FREECAD ASSEMBLY — COMPONENT RECIPES ("robot-main")

This assembly document has 11 components, labeled P0..P10 below (a component is one placed body or linked part). 6 of them carry a construction recipe — the FreeCAD feature program that regenerates the part from scratch, quoted from this document or its linked companion documents; the rest are supplied as boundary geometry only. No exploded tour is included for this assembly.
COMPONENT P0 — geometry summary ("traction-assy-l"; no construction recipe available for this part):
  bounding box: 33.4 x 17.5 x 10.2 mm
  tessellated surface: 1,796 triangles
  volume: 1266 mm^3 (21% of its bounding box)
  symmetry: mirror-symmetric across its y mid-plane
COMPONENT P1 — recipe-attached ("battery-t", a linked part whose construction recipe lives in a companion FreeCAD document of the same project; that document's serialized recipe follows).
Construction recipe (the companion document, serialized — sketch geometry with constraints, then the solid features built on it; lengths are millimeters unless a unit is written):

FCSTD DOCUMENT  (FreeCAD 0.21R33668 +7 (Git))
Label: BL-5C
License: All rights reserved
LicenseURL: https://en.wikipedia.org/wiki/All_rights_reserved
objects: Sketcher::SketchObject×2, PartDesign::Pad×1, PartDesign::Plane×1, PartDesign::Pocket×1, PartDesign::Body×1
note: 8 computed .brp shape members not serialized (recipe doc carries the construction recipe); baked Part::Feature solids carry a one-line shape summary decoded from their .brp

FEATURE [Sketcher::SketchObject] Sketch
  FullyConstrained = true
  MapMode = 5
  Placement = pos=(0,0,0) rot=(0.57735,0.57735,0.57735;2.0944rad)
  Support = -> [YZ_Plane]
  sketch-geometry (6):
    g0: ArcOfCircle CenterX=-14.15 CenterY=0 CenterZ=0 NormalX=0 NormalY=0 NormalZ=1 AngleXU=0 Radius=2.8 StartAngle=1.5708 EndAngle=4.71239
    g1: ArcOfCircle CenterX=14.15 CenterY=0 CenterZ=0 NormalX=0 NormalY=0 NormalZ=1 AngleXU=0 Radius=2.8 StartAngle=4.71239 EndAngle=7.85398
    g2: LineSegment StartX=-14.15 StartY=2.8 StartZ=0 EndX=14.15 EndY=2.8 EndZ=0
    g3: LineSegment StartX=-14.15 StartY=-2.8 StartZ=0 EndX=14.15 EndY=-2.8 EndZ=0
    g4: GeomPoint X=16.95 Y=0 Z=0
    g5: GeomPoint X=-16.95 Y=0 Z=0
  constraints (13):
    c: PointOnObject(g0,g-1)
    c: Horizontal(g2)
    c: Tangent(g2,g0) = 1.5708
    c: Tangent(g3,g0) = -1.5708
    c: Tangent(g3,g1) = -1.5708
    c: Tangent(g2,g1) = 1.5708
    c: PointOnObject(g4,g1)
    c: PointOnObject(g4,g-1)
    c: DistanceY(g1,g1) = 5.6
    c: Symmetric(g0,g1,g-1)
    c: PointOnObject(g5,g0)
    c: PointOnObject(g5,g-1)
    c: DistanceX(g5,g4) = 33.9
FEATURE [PartDesign::Pad] Pad
  Direction = (1,-2e-16,3e-16)
  Length = 53
  Length2 = 10
  Placement = pos=(0,0,0) rot=(0.57735,0.57735,0.57735;2.0944rad)
  Profile = -> Sketch
  ReferenceAxis = -> Sketch [N_Axis]
  Type = 0
FEATURE [PartDesign::Plane] DatumPlane
  Length = 60
  MapMode = 5
  Placement = pos=(0,0,0) rot=(0.57735,0.57735,-0.57735;4.18879rad)
  ResizeMode = 0
  Support = -> [Pad]
  Width = 60
FEATURE [Sketcher::SketchObject] Sketch001
  ExternalGeometry = -> [Pad]
  FullyConstrained = true
  MapMode = 5
  Placement = pos=(0,0,0) rot=(0.57735,0.57735,-0.57735;4.18879rad)
  Support = -> [DatumPlane]
  sketch-geometry (16):
    g0: LineSegment StartX=11.95 StartY=2.3 StartZ=0 EndX=13.95 EndY=2.3 EndZ=0
    g1: LineSegment StartX=13.95 StartY=2.3 StartZ=0 EndX=13.95 EndY=-2.3 EndZ=0
    g2: LineSegment StartX=13.95 StartY=-2.3 StartZ=0 EndX=11.95 EndY=-2.3 EndZ=0
    g3: LineSegment StartX=11.95 StartY=-2.3 StartZ=0 EndX=11.95 EndY=2.3 EndZ=0
    g4: LineSegment StartX=8.75 StartY=2.3 StartZ=0 EndX=10.75 EndY=2.3 EndZ=0
    g5: LineSegment StartX=10.75 StartY=2.3 StartZ=0 EndX=10.75 EndY=-2.3 EndZ=0
    g6: LineSegment StartX=10.75 StartY=-2.3 StartZ=0 EndX=8.75 EndY=-2.3 EndZ=0
    g7: LineSegment StartX=8.75 StartY=-2.3 StartZ=0 EndX=8.75 EndY=2.3 EndZ=0
    g8: LineSegment StartX=5.55 StartY=2.3 StartZ=0 EndX=7.55 EndY=2.3 EndZ=0
    g9: LineSegment StartX=7.55 StartY=2.3 StartZ=0 EndX=7.55 EndY=-2.3 EndZ=0
    g10: LineSegment StartX=7.55 StartY=-2.3 StartZ=0 EndX=5.55 EndY=-2.3 EndZ=0
    g11: LineSegment StartX=5.55 StartY=-2.3 StartZ=0 EndX=5.55 EndY=2.3 EndZ=0
    g12: LineSegment StartX=7.55 StartY=2.3 StartZ=0 EndX=8.75 EndY=2.3 EndZ=0
    g13: LineSegment StartX=10.75 StartY=2.3 StartZ=0 EndX=11.95 EndY=2.3 EndZ=0
    g14: GeomPoint X=-16.95 Y=0 Z=0
    g15: GeomPoint X=16.95 Y=0 Z=0
  constraints (43):
    c: Coincident(g0,g1)
    c: Coincident(g1,g2)
    c: Coincident(g2,g3)
    c: Coincident(g3,g0)
    c: Horizontal(g0)
    c: Horizontal(g2)
    c: Vertical(g3)
    c: Coincident(g4,g5)
    c: Coincident(g5,g6)
    c: Coincident(g6,g7)
    c: Coincident(g7,g4)
    c: Horizontal(g4)
    c: Horizontal(g6)
    c: Vertical(g5)
    c: Vertical(g7)
    c: Coincident(g8,g9)
    c: Coincident(g9,g10)
    c: Coincident(g10,g11)
    c: Coincident(g11,g8)
    c: Horizontal(g8)
    c: Horizontal(g10)
    c: Vertical(g9)
    c: Vertical(g11)
    c: PointOnObject(g4,g8)
    c: PointOnObject(g0,g8)
    c: PointOnObject(g6,g10)
    c: PointOnObject(g2,g10)
    c: Equal(g8,g4)
    c: Coincident(g12,g8)
    c: Coincident(g12,g4)
    c: Coincident(g13,g4)
    c: Coincident(g13,g0)
    c: Equal(g13,g12)
    c: PointOnObject(g14,g-3)
    c: PointOnObject(g14,g-1)
    c: DistanceX(g14,g10) = 22.5
    c: PointOnObject(g15,g-1)
    c: PointOnObject(g15,g-4)
    c: DistanceX(g1,g15) = 3
    c: DistanceX(g6,g6) = 2
    c: Equal(g2,g6)
    c: Symmetric(g0,g1,g-1)
    c: DistanceY(g1,g1) = 4.6
FEATURE [PartDesign::Pocket] Pocket
  BaseFeature = -> Pad
  Direction = (1,-4e-16,4e-16)
  Length = 0.6
  Length2 = 5
  Placement = pos=(0,0,0) rot=(0.57735,0.57735,0.57735;2.0944rad)
  Profile = -> Sketch001
  ReferenceAxis = -> Sketch001 [N_Axis]
  Type = 0
FEATURE [PartDesign::Body] Body  label="BL-5C"
  Group = -> [Sketch,Pad,DatumPlane,Sketch001,Pocket]
  Origin = -> Origin
  Tip = -> Pocket
COMPONENT P2 — same part as P1; its construction recipe is shown at P1.
COMPONENT P3 — recipe-attached ("pcb", a linked part whose construction recipe lives in a companion FreeCAD document of the same project; that document's serialized recipe follows).
Construction recipe (the companion document, serialized — sketch geometry with constraints, then the solid features built on it; lengths are millimeters unless a unit is written):

FCSTD DOCUMENT  (FreeCAD 0.21R33668 +7 (Git))
Label: robot-pcb
License: All rights reserved
LicenseURL: https://en.wikipedia.org/wiki/All_rights_reserved
objects: Part::Feature×12, App::Part×12, Sketcher::SketchObject×2, PartDesign::Pad×2, PartDesign::Body×2, App::LinkGroup×1
note: 20 computed .brp shape members not serialized (recipe doc carries the construction recipe); baked Part::Feature solids carry a one-line shape summary decoded from their .brp

FEATURE [Sketcher::SketchObject] Sketch004
  FullyConstrained = true
  MapMode = 5
  Support = -> [XY_Plane001]
  sketch-geometry (40):
    g0: LineSegment StartX=-32 StartY=20 StartZ=0 EndX=32 EndY=20 EndZ=0
    g1: LineSegment StartX=32 StartY=20 StartZ=0 EndX=32 EndY=-20 EndZ=0
    g2: LineSegment StartX=32 StartY=-20 StartZ=0 EndX=-32 EndY=-20 EndZ=0
    g3: LineSegment StartX=-32 StartY=-20 StartZ=0 EndX=-32 EndY=20 EndZ=0
    g4: LineSegment StartX=32 StartY=20 StartZ=0 EndX=32 EndY=-20 EndZ=0
    g5: ArcOfCircle CenterX=13 CenterY=-15 CenterZ=0 NormalX=0 NormalY=0 NormalZ=1 AngleXU=0 Radius=1.05 StartAngle=1.5708 EndAngle=4.71239
    g6: ArcOfCircle CenterX=30 CenterY=-15 CenterZ=0 NormalX=0 NormalY=0 NormalZ=1 AngleXU=0 Radius=1.05 StartAngle=4.71239 EndAngle=7.85398
    g7: LineSegment StartX=13 StartY=-16.05 StartZ=0 EndX=30 EndY=-16.05 EndZ=0
    g8: LineSegment StartX=30 StartY=-13.95 StartZ=0 EndX=13 EndY=-13.95 EndZ=0
    g9: ArcOfCircle CenterX=-30 CenterY=15 CenterZ=0 NormalX=0 NormalY=0 NormalZ=1 AngleXU=0 Radius=1.05 StartAngle=1.5708 EndAngle=4.71239
    g10: ArcOfCircle CenterX=-13 CenterY=15 CenterZ=0 NormalX=0 NormalY=0 NormalZ=1 AngleXU=0 Radius=1.05 StartAngle=4.71239 EndAngle=7.85398
    g11: LineSegment StartX=-30 StartY=13.95 StartZ=0 EndX=-13 EndY=13.95 EndZ=0
    g12: LineSegment StartX=-13 StartY=16.05 StartZ=0 EndX=-30 EndY=16.05 EndZ=0
    g13: LineSegment StartX=-32 StartY=-20 StartZ=0 EndX=-32 EndY=20 EndZ=0
    g14: ArcOfCircle CenterX=4 CenterY=15 CenterZ=0 NormalX=0 NormalY=0 NormalZ=1 AngleXU=0 Radius=1.05 StartAngle=1.5708 EndAngle=4.71239
    g15: ArcOfCircle CenterX=24 CenterY=15 CenterZ=0 NormalX=0 NormalY=0 NormalZ=1 AngleXU=0 Radius=1.05 StartAngle=4.71239 EndAngle=7.85398
    g16: LineSegment StartX=4 StartY=13.95 StartZ=0 EndX=24 EndY=13.95 EndZ=0
    g17: LineSegment StartX=24 StartY=16.05 StartZ=0 EndX=4 EndY=16.05 EndZ=0
    g18: ArcOfCircle CenterX=-24 CenterY=-15 CenterZ=0 NormalX=0 NormalY=0 NormalZ=1 AngleXU=0 Radius=1.05 StartAngle=1.5708 EndAngle=4.71239
    g19: ArcOfCircle CenterX=-4 CenterY=-15 CenterZ=0 NormalX=0 NormalY=0 NormalZ=1 AngleXU=0 Radius=1.05 StartAngle=4.71239 EndAngle=7.85398
    g20: LineSegment StartX=-24 StartY=-16.05 StartZ=0 EndX=-4 EndY=-16.05 EndZ=0
    g21: LineSegment StartX=-4 StartY=-13.95 StartZ=0 EndX=-24 EndY=-13.95 EndZ=0
    g22: ArcOfCircle CenterX=-61 CenterY=0 CenterZ=0 NormalX=0 NormalY=0 NormalZ=1 AngleXU=0 Radius=29 StartAngle=5.75173 EndAngle=6.81464
    g23: LineSegment StartX=-36 StartY=14.6969 StartZ=0 EndX=-36 EndY=20 EndZ=0
    g24: LineSegment StartX=-32 StartY=20 StartZ=0 EndX=-36 EndY=20 EndZ=0
    g25: LineSegment StartX=-36 StartY=-14.6969 StartZ=0 EndX=-36 EndY=-20 EndZ=0
    g26: LineSegment StartX=-32 StartY=-20 StartZ=0 EndX=-36 EndY=-20 EndZ=0
    g27: ArcOfCircle CenterX=61 CenterY=0 CenterZ=0 NormalX=0 NormalY=0 NormalZ=1 AngleXU=0 Radius=29 StartAngle=2.61013 EndAngle=3.67305
    g28: LineSegment StartX=32 StartY=20 StartZ=0 EndX=36 EndY=20 EndZ=0
    g29: LineSegment StartX=36 StartY=20 StartZ=0 EndX=36 EndY=14.6969 EndZ=0
    g30: LineSegment StartX=32 StartY=-20 StartZ=0 EndX=36 EndY=-20 EndZ=0
    g31: LineSegment StartX=36 StartY=-20 StartZ=0 EndX=36 EndY=-14.6969 EndZ=0
    g32: Circle CenterX=-33.5 CenterY=-17.5 CenterZ=0 NormalX=0 NormalY=0 NormalZ=1 AngleXU=0 Radius=1.3
    g33: Circle CenterX=-33.5 CenterY=17.5 CenterZ=0 NormalX=0 NormalY=0 NormalZ=1 AngleXU=0 Radius=1.3
    g34: Circle CenterX=33.5 CenterY=17.5 CenterZ=0 NormalX=0 NormalY=0 NormalZ=1 AngleXU=0 Radius=1.3
    g35: Circle CenterX=33.5 CenterY=-17.5 CenterZ=0 NormalX=0 NormalY=0 NormalZ=1 AngleXU=0 Radius=1.3
    g36: LineSegment StartX=-33.5 StartY=17.5 StartZ=0 EndX=33.5 EndY=17.5 EndZ=0
    g37: LineSegment StartX=33.5 StartY=17.5 StartZ=0 EndX=33.5 EndY=-17.5 EndZ=0
    g38: LineSegment StartX=33.5 StartY=-17.5 StartZ=0 EndX=-33.5 EndY=-17.5 EndZ=0
    g39: LineSegment StartX=-33.5 StartY=-17.5 StartZ=0 EndX=-33.5 EndY=17.5 EndZ=0
  constraints (104):
    c: Coincident(g0,g1)
    c: Coincident(g1,g2)
    c: Coincident(g2,g3)
    c: Coincident(g3,g0)
    c: Horizontal(g0)
    c: Horizontal(g2)
    c: Vertical(g1)
    c: Vertical(g3)
    c: Symmetric(g0,g1,g-1)
    c: DistanceY(g1,g1) = 40
    c: DistanceX(g0,g0) = 64
    c: Coincident(g4,g2)
    c: Tangent(g5,g7) = -1.5708
    c: Tangent(g7,g6) = -1.5708
    c: Tangent(g6,g8) = -1.5708
    c: Tangent(g8,g5) = -1.5708
    c: Equal(g5,g6)
    c: Horizontal(g7)
    c: DistanceX(g5,g6) = 17
    c: DistanceY(g2,g6) = 5
    c: DistanceY(g5,g5) = 2.1
    c: DistanceX(g6,g2) = 2
    c: Tangent(g9,g11) = -1.5708
    c: Tangent(g11,g10) = -1.5708
    c: Tangent(g10,g12) = -1.5708
    c: Tangent(g12,g9) = -1.5708
    c: Equal(g9,g10)
    c: Horizontal(g11)
    c: Equal(g10,g5)
    c: Symmetric(g9,g6,g-1)
    c: Coincident(g13,g0)
    c: DistanceY(g10,g10) = 2.1
    c: DistanceY(g6,g0) = 35
    c: Coincident(g13,g2)
    c: Coincident(g4,g0)
    c: Tangent(g14,g16) = -1.5708
    c: Tangent(g16,g15) = -1.5708
    c: Tangent(g15,g17) = -1.5708
    c: Tangent(g17,g14) = -1.5708
    c: Equal(g14,g15)
    c: Horizontal(g16)
    c: Tangent(g18,g20) = -1.5708
    c: Tangent(g20,g19) = -1.5708
    c: Tangent(g19,g21) = -1.5708
    c: Tangent(g21,g18) = -1.5708
    c: Equal(g18,g19)
    c: Horizontal(g20)
    c: Equal(g19,g10)
    c: Equal(g14,g10)
    c: PointOnObject(g14,g12)
    c: Symmetric(g18,g15,g-1)
    c: DistanceX(g2,g18) = 8
    c: PointOnObject(g22,g-1)
    c: Tangent(g22,g13)
    c: Diameter(g22) = 58
    c: Coincident(g23,g22)
    c: Vertical(g23)
    c: Coincident(g24,g0)
    c: Coincident(g24,g23)
    c: Coincident(g25,g22)
    c: Vertical(g25)
    c: Coincident(g26,g2)
    c: Coincident(g26,g25)
    c: Horizontal(g26)
    c: Horizontal(g24)
    c: Equal(g24,g26)
    c: DistanceX(g26,g26) = 4
    c: PointOnObject(g27,g-1)
    c: Tangent(g27,g4)
    c: Coincident(g0,g28)
    c: Horizontal(g28)
    c: Coincident(g28,g29)
    c: Coincident(g29,g27)
    c: Vertical(g29)
    c: Coincident(g2,g30)
    c: Horizontal(g30)
    c: Coincident(g30,g31)
    c: Coincident(g31,g27)
    c: Vertical(g31)
    c: Equal(g30,g28)
    c: Diameter(g27) = 58
    c: DistanceX(g30,g30) = 4
    c: Coincident(g36,g37)
    c: Coincident(g37,g38)
    c: Coincident(g38,g39)
    c: Coincident(g39,g36)
    c: Horizontal(g36)
    c: Horizontal(g38)
    c: Vertical(g37)
    c: Vertical(g39)
    c: Coincident(g36,g33)
    c: Coincident(g37,g35)
    c: Coincident(g36,g34)
    c: Coincident(g38,g32)
    c: Symmetric(g32,g34,g-1)
    c: Diameter(g33) = 2.6
    c: Equal(g35,g32)
    c: Equal(g32,g34)
    c: Equal(g34,g33)
    c: DistanceX(g36,g36) = 67
    c: DistanceY(g39,g39) = 35
    c: Equal(g21,g17)
    c: Equal(g12,g8)
    c: DistanceX(g14,g15) = 20
FEATURE [PartDesign::Pad] Pad005
  Direction = (0,0,1)
  Length = 1.6
  Length2 = 10
  Profile = -> Sketch004
  ReferenceAxis = -> Sketch004 [N_Axis]
  Type = 0
FEATURE [PartDesign::Body] Body001  label="motor-pcb"
  Group = -> [Sketch004,Pad005]
  Origin = -> Origin001
  Placement = pos=(0,0,7) rot=(0,0,1;0rad)
  Tip = -> Pad005
FEATURE [Sketcher::SketchObject] Sketch005
  FullyConstrained = true
  MapMode = 5
  Support = -> [XY_Plane002]
  sketch-geometry (4):
    g0: LineSegment StartX=-32 StartY=20 StartZ=0 EndX=32 EndY=20 EndZ=0
    g1: LineSegment StartX=32 StartY=20 StartZ=0 EndX=32 EndY=-20 EndZ=0
    g2: LineSegment StartX=32 StartY=-20 StartZ=0 EndX=-32 EndY=-20 EndZ=0
    g3: LineSegment StartX=-32 StartY=-20 StartZ=0 EndX=-32 EndY=20 EndZ=0
  constraints (11):
    c: Coincident(g0,g1)
    c: Coincident(g1,g2)
    c: Coincident(g2,g3)
    c: Coincident(g3,g0)
    c: Horizontal(g0)
    c: Horizontal(g2)
    c: Vertical(g1)
    c: Vertical(g3)
    c: Symmetric(g0,g1,g-1)
    c: DistanceY(g1,g1) = 40
    c: DistanceX(g0,g0) = 64
FEATURE [PartDesign::Pad] Pad006
  Direction = (0,0,1)
  Length = 1.6
  Length2 = 10
  Profile = -> Sketch005
  ReferenceAxis = -> Sketch005 [N_Axis]
  Type = 0
FEATURE [PartDesign::Body] Body002  label="logic-pcb"
  Group = -> [Sketch005,Pad006]
  Origin = -> Origin002
  Placement = pos=(0,0,-7) rot=(0,1,0;3.14159rad)
  Tip = -> Pad006
FEATURE [Part::Feature] Part__Feature016  label="SOLID012"
  shape: bbox 11.3 x 3.89 x 7.705 mm, 815 faces (baked)
FEATURE [App::Part] usb4110_gf_a  label="usb4110-gf-a"
  Group = -> [Part__Feature016]
  Origin = -> Origin018
  Placement = pos=(118,-99.7499,1.65) rot=(0.57735,-0.57735,-0.57735;2.0944rad)
FEATURE [Part::Feature] Part__Feature017  label="COMPOUND003"
  shape: bbox 5.208 x 5.208 x 3.99 mm, 21 faces, 4 solids (baked)
FEATURE [App::Part] IND_SWPA5040S_SNL
  Group = -> [Part__Feature017]
  Origin = -> Origin019
  Placement = pos=(145.25,-101.75,1.65) rot=(0,0,-1;1.5708rad)
FEATURE [Part::Feature] Part__Feature018  label="SOLID013"
  shape: bbox 15.43 x 2.05 x 5.11 mm, 404 faces (baked)
FEATURE [App::Part] c_2_1734839_0_c_3d  label="c-2-1734839-0-c-3d"
  Group = -> [Part__Feature018]
  Origin = -> Origin020
  Placement = pos=(178.812,-99.9999,2.65) rot=(0.57735,0.57735,0.57735;2.0944rad)
FEATURE [Part::Feature] Part__Feature019  label="COMPOUND004"
  shape: bbox 5.589 x 2.947 x 1.1 mm, 32 faces, 4 solids (baked)
FEATURE [App::Part] SDO_B120AF_DIO
  Group = -> [Part__Feature019]
  Origin = -> Origin021
  Placement = pos=(151.5,-97.9999,1.65) rot=(0,0,1;3.14159rad)
FEATURE [Part::Feature] Part__Feature020  label="PCB001"
  shape: bbox 72 x 40 x 1.6 mm, 354 faces (baked)
FEATURE [App::Part] nanoInvaderBot_logic_1  label="nanoInvaderBot-logic 1"
  Group = -> [usb4110_gf_a,IND_SWPA5040S_SNL,c_2_1734839_0_c_3d,SDO_B120AF_DIO,Part__Feature020]
  Origin = -> Origin022
  Placement = pos=(-150,100,-9.1) rot=(0,0,1;0rad)
FEATURE [Part::Feature] Part__Feature  label="SOLID"
  shape: bbox 12.8 x 7 x 6.5 mm, 111 faces (baked)
FEATURE [App::Part] c_1746142_01_o1_3d  label="c-1746142-01-o1-3d"
  Group = -> [Part__Feature]
  Origin = -> Origin
  Placement = pos=(122.75,-109.8,1.65) rot=(0.57735,0.57735,0.57735;2.0944rad)
FEATURE [Part::Feature] Part__Feature021  label="COMPOUND"
  shape: bbox 5.208 x 5.208 x 3.99 mm, 21 faces, 4 solids (baked)
FEATURE [App::Part] IND_SWPA5040S_SNL001
  Group = -> [Part__Feature021]
  Origin = -> Origin023
  Placement = pos=(145.25,-101.75,-0.05) rot=(0.707107,-0.707107,0;3.14159rad)
FEATURE [Part::Feature] Part__Feature022  label="COMPOUND005"
  shape: bbox 12 x 3.701 x 6.501 mm, 163 faces, 15 solids (baked)
FEATURE [App::Part] S6B_ZR_SM4A_TF_LF__SN_  label="S6B-ZR-SM4A-TF_LF__SN_"
  Group = -> [Part__Feature022]
  Origin = -> Origin024
  Placement = pos=(166.5,-108.65,-0.05) rot=(-1,0,0;1.5708rad)
FEATURE [Part::Feature] Part__Feature023  label="COMPOUND006"
  shape: bbox 12 x 3.701 x 6.501 mm, 163 faces, 15 solids (baked)
FEATURE [App::Part] S6B_ZR_SM4A_TF_LF__SN_001  label="S6B-ZR-SM4A-TF_LF__SN_001"
  Group = -> [Part__Feature023]
  Origin = -> Origin025
  Placement = pos=(133.5,-91.3499,-0.05) rot=(0,0.707107,-0.707107;3.14159rad)
FEATURE [Part::Feature] Part__Feature024  label="SOLID014"
  shape: bbox 15.43 x 2.05 x 5.11 mm, 404 faces (baked)
FEATURE [App::Part] c_2_1734839_0_c_3d001  label="c-2-1734839-0-c-3d001"
  Group = -> [Part__Feature024]
  Origin = -> Origin026
  Placement = pos=(178.812,-99.9999,-1.05) rot=(0.57735,-0.57735,0.57735;4.18879rad)
FEATURE [Part::Feature] Part__Feature025  label="COMPOUND007"
  shape: bbox 5.589 x 2.947 x 1.1 mm, 32 faces, 4 solids (baked)
FEATURE [App::Part] SDO_B120AF_DIO001
  Group = -> [Part__Feature025]
  Origin = -> Origin027
  Placement = pos=(151.5,-97.9999,-0.05) rot=(1,0,0;3.14159rad)
FEATURE [Part::Feature] Part__Feature026  label="PCB"
  shape: bbox 72 x 40 x 1.6 mm, 354 faces (baked)
FEATURE [App::Part] nanoInvaderBot_power_1  label="nanoInvaderBot-power 1"
  Group = -> [c_1746142_01_o1_3d,IND_SWPA5040S_SNL001,S6B_ZR_SM4A_TF_LF__SN_,S6B_ZR_SM4A_TF_LF__SN_001,c_2_1734839_0_c_3d001,SDO_B120AF_DIO001,Part__Feature026]
  Origin = -> Origin028
  Placement = pos=(-150,100,7.5) rot=(0,0,1;0rad)
FEATURE [App::LinkGroup] LinkGroup  label="pcb-assy"
  ElementList = -> [Body002,Body001,nanoInvaderBot_logic_1,nanoInvaderBot_power_1]
  LinkMode = 1
COMPONENT P4 — recipe-attached ("track-l", a linked part whose construction recipe lives in a companion FreeCAD document of the same project; that document's serialized recipe follows).
Construction recipe (the companion document, serialized — sketch geometry with constraints, then the solid features built on it; lengths are millimeters unless a unit is written):

FCSTD DOCUMENT  (FreeCAD 0.21R33668 +7 (Git))
Label: GT2-220
License: All rights reserved
LicenseURL: https://en.wikipedia.org/wiki/All_rights_reserved
objects: Sketcher::SketchObject×1, PartDesign::Pad×1, PartDesign::Body×1
note: 4 computed .brp shape members not serialized (recipe doc carries the construction recipe); baked Part::Feature solids carry a one-line shape summary decoded from their .brp

FEATURE [Sketcher::SketchObject] Sketch
  FullyConstrained = true
  MapMode = 5
  Placement = pos=(0,0,0) rot=(1,0,0;1.5708rad)
  Support = -> [XZ_Plane]
  sketch-geometry (10):
    g0: ArcOfCircle CenterX=0 CenterY=0 CenterZ=0 NormalX=0 NormalY=0 NormalZ=1 AngleXU=0 Radius=18 StartAngle=1.5708 EndAngle=4.71239
    g1: ArcOfCircle CenterX=47.6 CenterY=0 CenterZ=0 NormalX=0 NormalY=0 NormalZ=1 AngleXU=0 Radius=18 StartAngle=4.71239 EndAngle=7.85398
    g2: LineSegment StartX=1.1e-15 StartY=18 StartZ=0 EndX=47.6 EndY=18 EndZ=0
    g3: LineSegment StartX=-3.3e-15 StartY=-18 StartZ=0 EndX=47.6 EndY=-18 EndZ=0
    g4: Circle CenterX=0 CenterY=0 CenterZ=0 NormalX=0 NormalY=0 NormalZ=1 AngleXU=0 Radius=17
    g5: GeomPoint X=0 Y=17 Z=0
    g6: ArcOfCircle CenterX=0 CenterY=0 CenterZ=0 NormalX=0 NormalY=0 NormalZ=1 AngleXU=0 Radius=16.25 StartAngle=1.5708 EndAngle=4.71239
    g7: ArcOfCircle CenterX=47.6 CenterY=0 CenterZ=0 NormalX=0 NormalY=0 NormalZ=1 AngleXU=0 Radius=16.25 StartAngle=4.71239 EndAngle=7.85398
    g8: LineSegment StartX=1e-15 StartY=16.25 StartZ=0 EndX=47.6 EndY=16.25 EndZ=0
    g9: LineSegment StartX=-3e-15 StartY=-16.25 StartZ=0 EndX=47.6 EndY=-16.25 EndZ=0
  constraints (22):
    c: Coincident(g0,g-1)
    c: PointOnObject(g0,g-2)
    c: PointOnObject(g1,g-1)
    c: Coincident(g4,g0)
    c: PointOnObject(g5,g4)
    c: PointOnObject(g5,g-2)
    c: DistanceY(g5,g0) = 1
    c: DistanceX(g0,g1) = 47.6
    c: DistanceX(g0,g1) = 47.6
    c: Tangent(g2,g1) = 1.5708
    c: Tangent(g3,g1) = -1.5708
    c: Tangent(g3,g0) = -1.5708
    c: Tangent(g2,g0) = 1.5708
    c: Diameter(g4) = 34
    c: Coincident(g6,g0)
    c: PointOnObject(g6,g-2)
    c: Coincident(g7,g1)
    c: Tangent(g9,g7) = -1.5708
    c: Tangent(g8,g7) = 1.5708
    c: Tangent(g8,g6) = 1.5708
    c: Tangent(g9,g6) = -1.5708
    c: DistanceY(g6,g5) = 0.75
FEATURE [PartDesign::Pad] Pad
  Direction = (0,-1,-2e-16)
  Length = 15
  Length2 = 10
  Midplane = true
  Placement = pos=(0,0,0) rot=(1,0,0;1.5708rad)
  Profile = -> Sketch
  ReferenceAxis = -> Sketch [N_Axis]
  Type = 0
FEATURE [PartDesign::Body] Body  label="GT2-220"
  Group = -> [Sketch,Pad]
  Origin = -> Origin
  Tip = -> Pad
COMPONENT P5 — same part as P4; its construction recipe is shown at P4.
COMPONENT P6 — recipe-attached ("tt-ball", a linked part whose construction recipe lives in a companion FreeCAD document of the same project; that document's serialized recipe follows).
Construction recipe (the companion document, serialized — sketch geometry with constraints, then the solid features built on it; lengths are millimeters unless a unit is written):

FCSTD DOCUMENT  (FreeCAD 0.21R33668 +7 (Git))
Label: ball
License: All rights reserved
LicenseURL: https://en.wikipedia.org/wiki/All_rights_reserved
objects: Sketcher::SketchObject×1, PartDesign::Revolution×1, PartDesign::Body×1
note: 4 computed .brp shape members not serialized (recipe doc carries the construction recipe); baked Part::Feature solids carry a one-line shape summary decoded from their .brp

FEATURE [Sketcher::SketchObject] Sketch
  FullyConstrained = true
  MapMode = 5
  Placement = pos=(0,0,0) rot=(1,0,0;1.5708rad)
  Support = -> [XZ_Plane]
  sketch-geometry (2):
    g0: ArcOfCircle CenterX=0 CenterY=0 CenterZ=0 NormalX=0 NormalY=0 NormalZ=1 AngleXU=0 Radius=20 StartAngle=1.5708 EndAngle=4.71239
    g1: LineSegment StartX=0 StartY=20 StartZ=0 EndX=0 EndY=-20 EndZ=0
  constraints (6):
    c: Coincident(g0,g-1)
    c: Coincident(g1,g0)
    c: Coincident(g1,g0)
    c: Vertical(g1)
    c: PointOnObject(g0,g1)
    c: DistanceY(g1,g1) = 40
FEATURE [PartDesign::Revolution] Revolution
  Angle = 360
  Axis = (0,2e-16,1)
  Base = (0,0,0)
  Placement = pos=(0,0,0) rot=(1,0,0;1.5708rad)
  Profile = -> Sketch
  ReferenceAxis = -> Sketch [V_Axis]
FEATURE [PartDesign::Body] Body  label="ball"
  Group = -> [Sketch,Revolution]
  Origin = -> Origin
  Tip = -> Revolution
COMPONENT P7 — geometry summary ("body-main"; no construction recipe available for this part):
  bounding box: 71.8 x 40.0 x 36.0 mm
  tessellated surface: 868 triangles
  volume: 22640 mm^3 (22% of its bounding box)
  symmetry: 2-fold rotationally symmetric about the x axis
COMPONENT P8 — geometry summary ("idler-assy-l"; no construction recipe available for this part):
  bounding box: 34.0 x 34.0 x 24.0 mm
  tessellated surface: 7,350 triangles
  volume: 8429 mm^3 (30% of its bounding box)
  symmetry: mirror-symmetric across its z mid-plane
COMPONENT P9 — geometry summary ("idler-assy-r"; no construction recipe available for this part):
  bounding box: 34.0 x 34.0 x 24.0 mm
  tessellated surface: 7,350 triangles
  volume: 8429 mm^3 (30% of its bounding box)
  symmetry: mirror-symmetric across its z mid-plane
COMPONENT P10 — geometry summary ("traction-assy-r"; no construction recipe available for this part):
  bounding box: 33.4 x 17.5 x 10.2 mm
  tessellated surface: 1,796 triangles
  volume: 1266 mm^3 (21% of its bounding box)
  symmetry: mirror-symmetric across its y mid-plane
PROVENANCE & LICENSES
A FreeCAD (.FCStd) document from a public repository crawl; recipes are the document's own serialized feature recipes (and, for linked parts, companion documents' recipes).
License: gpl-3.0.
